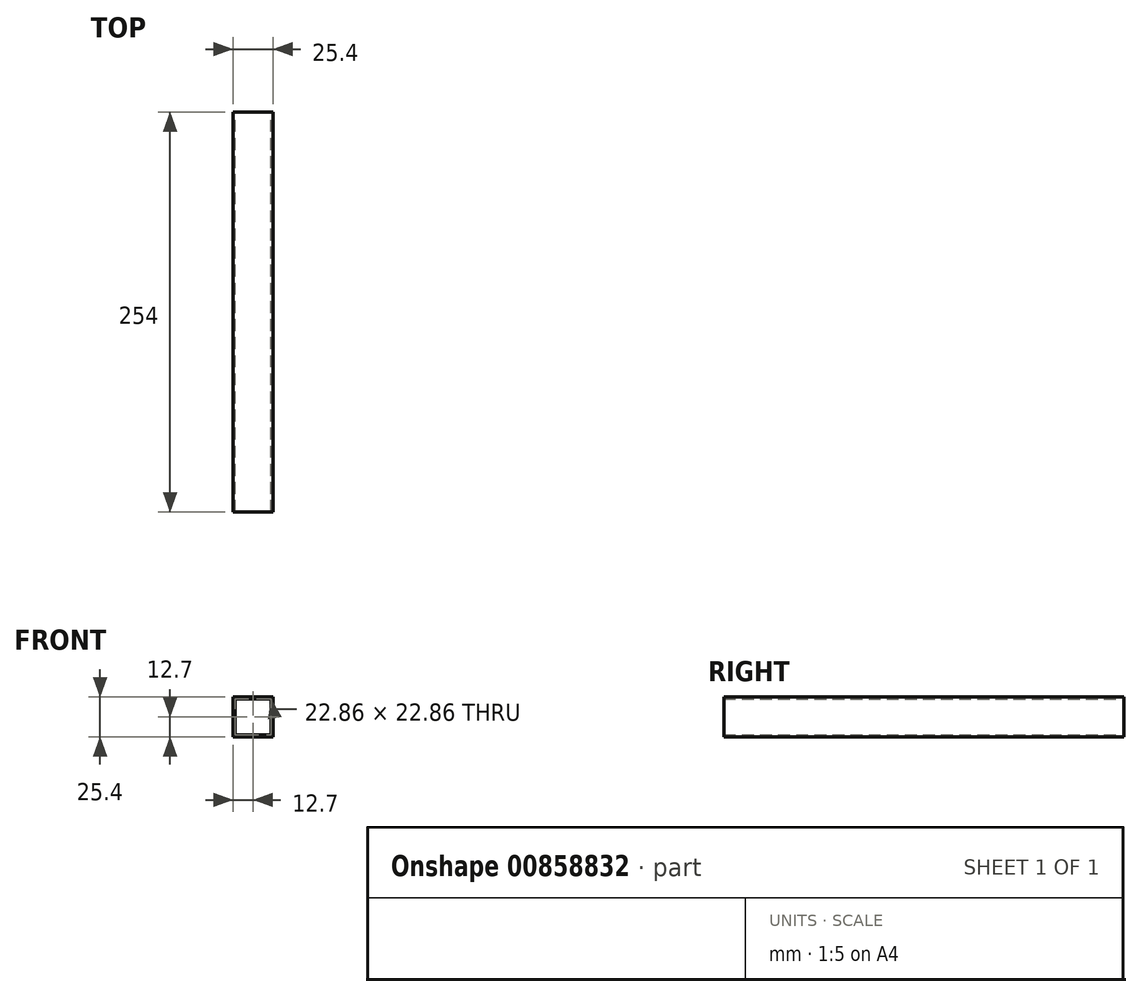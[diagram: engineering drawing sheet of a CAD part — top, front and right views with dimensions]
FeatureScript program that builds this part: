
annotation { "Feature Type Name" : "Feature", "Feature Type Description" : "" }
export const myFeature = defineFeature(function(context is Context, id is Id, definition is map)
    precondition{}
    {
        {
            var Q0;
            Q0=qCreatedBy(makeId("Front.planeOp"),FACE);
            var sketch = newSketch(context, id + "F0", { "sketchPlane" : qUnion([Q0])});
            skLineSegment(sketch, "E0.bottom", {"start": v(12.7, 12.7) * mm, "end": v(-12.7, 12.7) * mm});
            skLineSegment(sketch, "E0.top", {"start": v(12.7, -12.7) * mm, "end": v(-12.7, -12.7) * mm});
            skLineSegment(sketch, "E0.left", {"start": v(12.7, 12.7) * mm, "end": v(12.7, -12.7) * mm});
            skLineSegment(sketch, "E0.right", {"start": v(-12.7, 12.7) * mm, "end": v(-12.7, -12.7) * mm});
            skPoint(sketch, "E0.middle", {"position": v(0, 0) * mm});
            skLineSegment(sketch, "E1.bottom", {"start": v(11.43, 11.43) * mm, "end": v(-11.43, 11.43) * mm});
            skLineSegment(sketch, "E1.top", {"start": v(11.43, -11.43) * mm, "end": v(-11.43, -11.43) * mm});
            skLineSegment(sketch, "E1.left", {"start": v(11.43, 11.43) * mm, "end": v(11.43, -11.43) * mm});
            skLineSegment(sketch, "E1.right", {"start": v(-11.43, 11.43) * mm, "end": v(-11.43, -11.43) * mm});
            skSolve(sketch);
        }
        {
            var Q0;
            Q0 = qSketchRegion(id + "F0", true);
            extrude(context, id + "F1", {"entities" : qUnion([Q0]), "depth" : 254 * mm, "offsetDistance" : 25.4 * mm});
        }
    });
